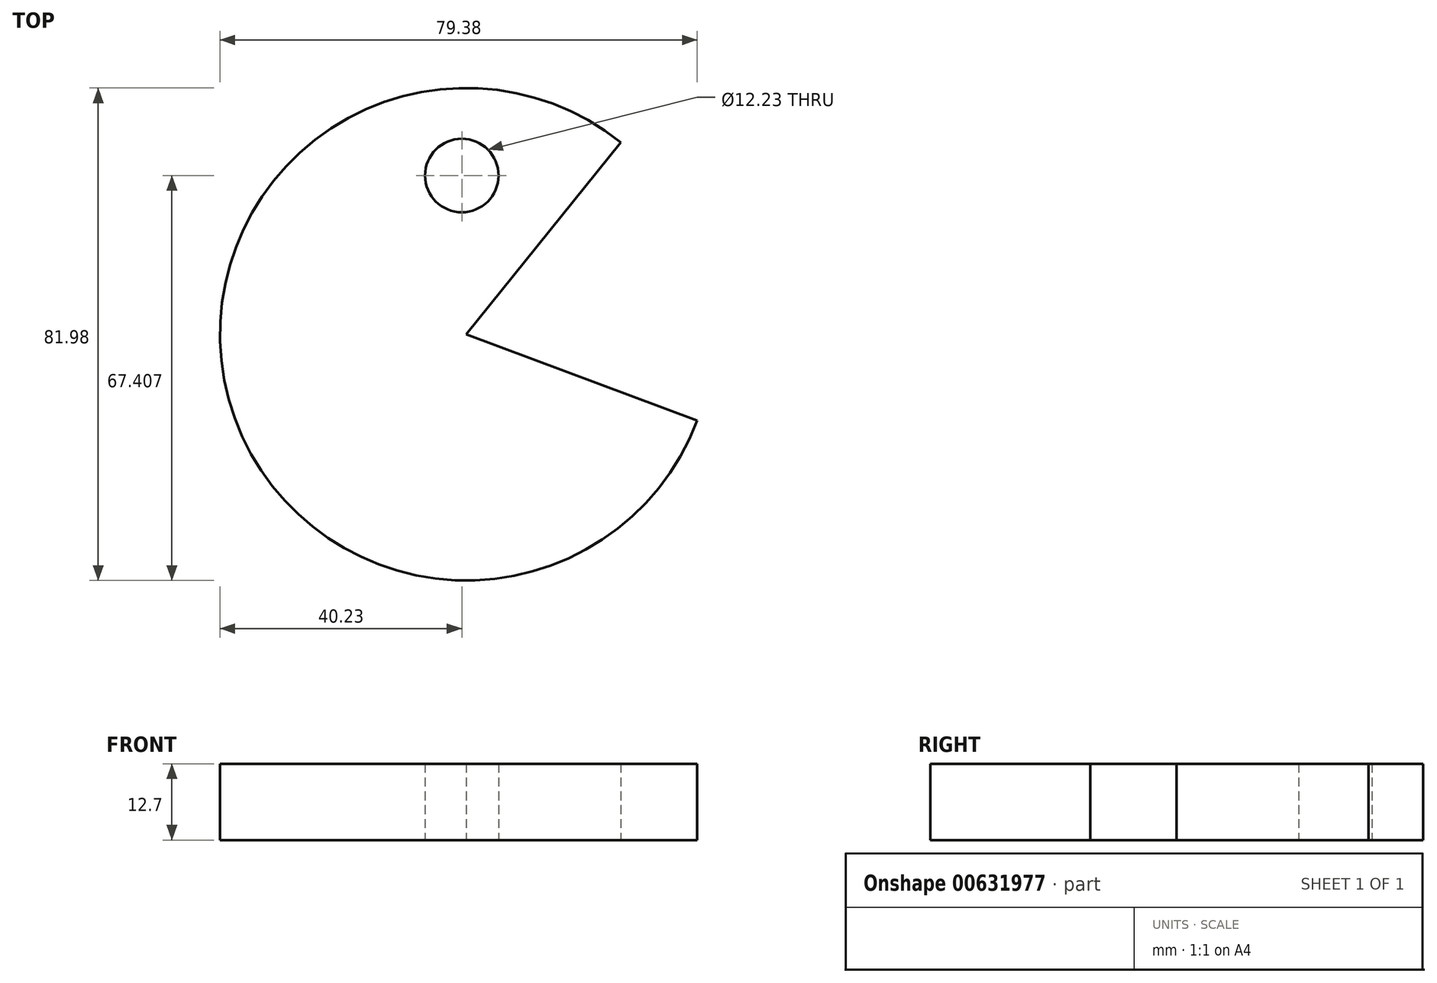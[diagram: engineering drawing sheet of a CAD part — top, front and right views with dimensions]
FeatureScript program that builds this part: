
annotation { "Feature Type Name" : "Feature", "Feature Type Description" : "" }
export const myFeature = defineFeature(function(context is Context, id is Id, definition is map)
    precondition{}
    {
        {
            var Q0;
            Q0=qCreatedBy(makeId("Top.planeOp"),FACE);
            var sketch = newSketch(context, id + "F0", { "sketchPlane" : qUnion([Q0])});
            skArc(sketch, "E0", {"start": v(25.67, 31.95) * mm, "mid": v(-39.53, -10.85) * mm, "end": v(38.39, -14.37) * mm});
            skLineSegment(sketch, "E1", {"start": v(25.67, 31.95) * mm, "end": v(0, 0) * mm});
            skLineSegment(sketch, "E2", {"start": v(0, 0) * mm, "end": v(38.39, -14.37) * mm});
            skCircle(sketch, "E3", {"center": v(-0.76, 26.42) * mm, "radius": 6.11 * mm});
            skSolve(sketch);
        }
        {
            var Q0;
            Q0=makeQuery(id+"F0.imprint","IMPRINT",FACE,{"disambiguationData":[TD([[makeQuery(id+"F0.imprint","IMPRINT",EDGE,{"derivedFrom":sQuery(id+"F0.wireOp",EDGE,"E0")}),1.0]])]});
            extrude(context, id + "F1", {"entities" : qUnion([Q0]), "depth" : 12.7 * mm, "offsetDistance" : 25.4 * mm});
        }
    });
